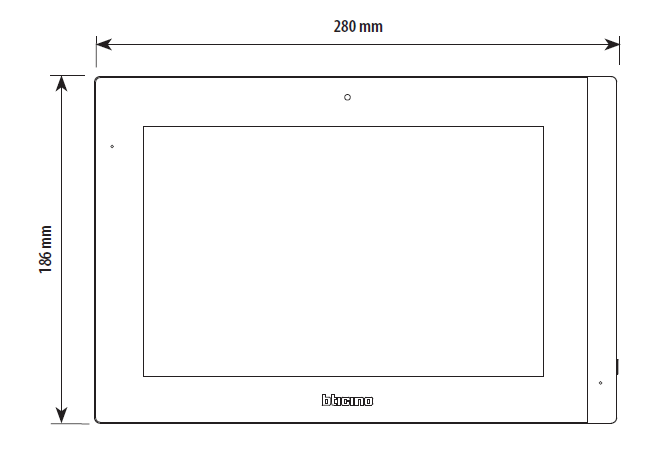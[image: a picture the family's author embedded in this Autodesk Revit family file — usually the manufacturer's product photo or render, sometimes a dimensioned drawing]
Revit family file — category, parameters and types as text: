
# Revit family: BERSfr_65_COM_UN_Bticino Classe 300EOS Poste Interieur_Legrand
name_source: partatom
category: Communication Devices
units: mm (PartAtom-declared; Revit-internal decimal feet)

## family parameters
Always vertical = No
Cut with Voids When Loaded = No
Maintain Annotation Orientation = No
Part Type = Normal
Room Calculation Point = No
Round Connector Dimension = Use Diameter
Shared = No
Work Plane-Based = No

## types (1)
- Classe 300EOS
    Avec video = Yes
    BERSfr_C_LE_Hauteur = 222 mm
    BERSfr_C_LE_Largeur = 121 mm  [stored 0.396982 ft]
    BERSfr_C_LE_Profondeur = 32 mm  [stored 0.104987 ft]
    BERSfr_C_MA_Matiere = BERSfr_FME_n6 PVC blanc_Legrand
    BERSfr_C_MA_Matiere01 = BERSfr_FME_n6 PVC blanc_Legrand
    BERSfr_C_MA_Matiere02 = BERSfr_FME_o2 Verre noir_Legrand
    BERSfr_C_TX_CodeArticle = BT-344842
    BERSfr_C_TX_CodeClasseIP = 54
    BERSfr_C_TX_CodeETIM = EC001101
    BERSfr_C_TX_CodeFournisseurGln = 541475999983
    BERSfr_C_TX_CodeGtin = 8005543677513
    BERSfr_C_TX_CodeProduit = BT-344842
    BERSfr_C_TX_DateDeSortieContenu = 12-1-2022
    BERSfr_C_TX_Description = POSTE INTERIEUR CLASSE 300EOS WITH NETATMO BOUCLE Inductive
    BERSfr_C_TX_Type = Systèmes de communication
    BERSfr_C_UR_CodeETIM = https://prod.etim-international.com
    Bouton ouverture porte = Yes
    Camera = Sans Caméra
    Default Elevation = 0 mm  [stored 0 ft]
    Description = POSTE INTERIEUR CLASSE 300EOS WITH NETATMO BOUCLE Inductive
    Ecran Tactile = Yes
    IfcDescription = POSTE INTERIEUR CLASSE 300EOS WITH NETATMO BOUCLE Inductive
    IfcExportAs = IfcAudioVisualApplianceType
    IfcExportType = TELEPHONE
    Manufacturer = Legrand
    Mode de pose = saillie
    Model = Class 300 V13E
    Objet Connecté = Yes
    Résolution écran = 1280x720
    Taille de l'écran (Pouces) = 5
    Temperature d'utilisation MIN-MAX = +5/+40 °C
    Type d'interface = Wi-Fi/ RJ45
    Type de raccordement = système bus
    URL = https://ecataleg.be

note: [stored X ft] marks values corroborated as IEEE doubles in the binary element streams (Revit-internal decimal feet)

## geometry (parser evidence)
native form markers: Sweep x4
no freeform markers — native parametric forms only
